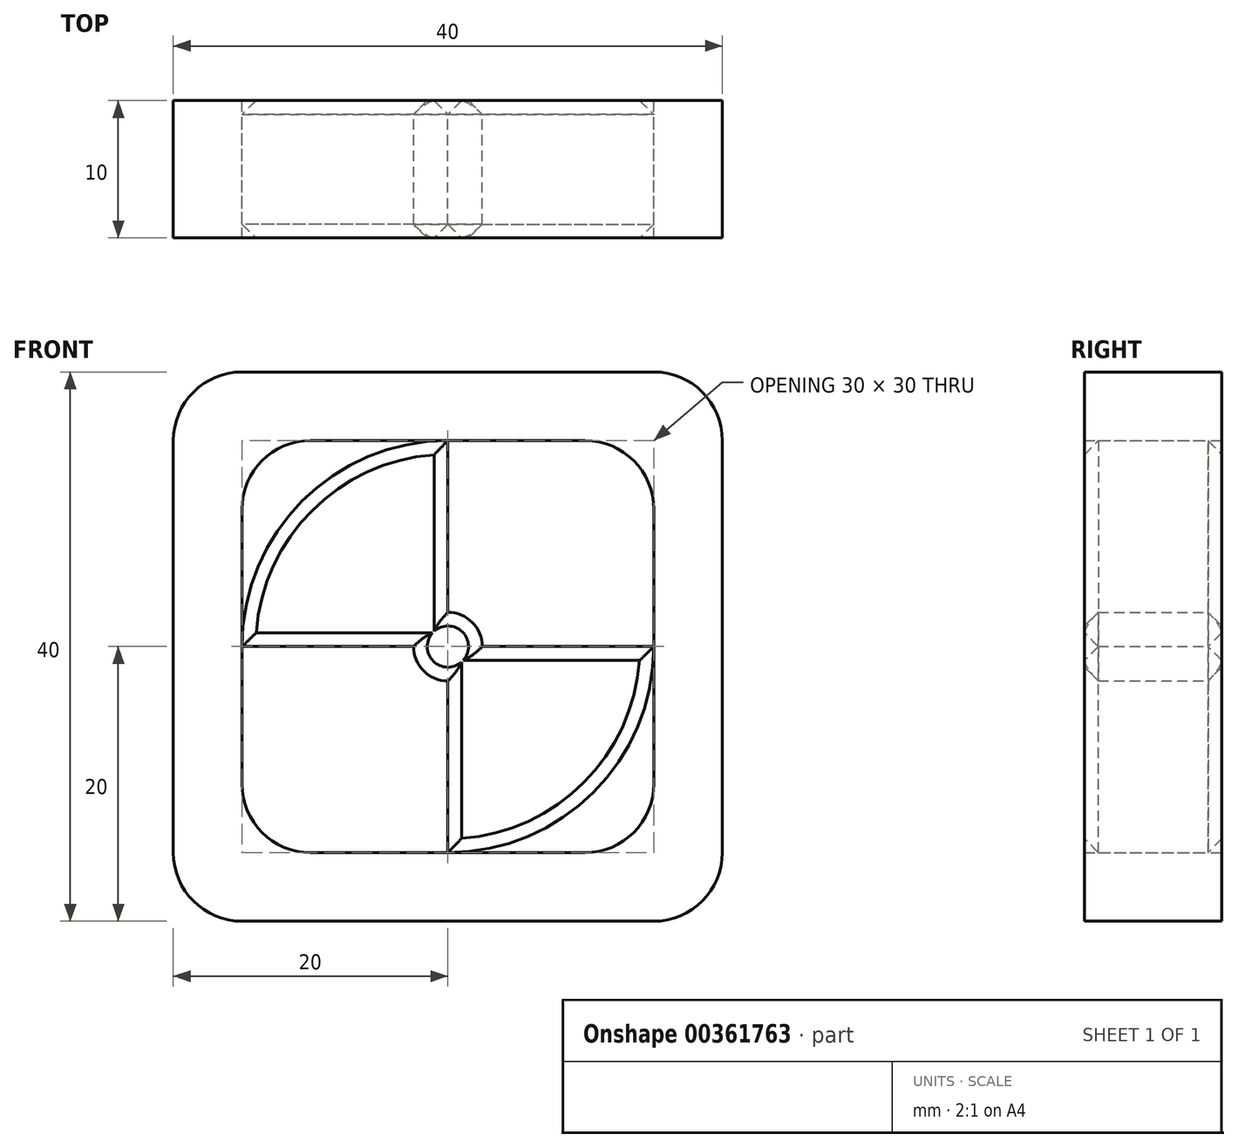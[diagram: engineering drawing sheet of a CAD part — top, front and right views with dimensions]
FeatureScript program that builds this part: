
annotation { "Feature Type Name" : "Feature", "Feature Type Description" : "" }
export const myFeature = defineFeature(function(context is Context, id is Id, definition is map)
    precondition{}
    {
        {
            var Q0;
            Q0=qCreatedBy(makeId("Front.planeOp"),FACE);
            var sketch = newSketch(context, id + "F0", { "sketchPlane" : qUnion([Q0])});
            skLineSegment(sketch, "E0.bottom", {"start": v(15, 15) * mm, "end": v(-15, 15) * mm});
            skLineSegment(sketch, "E0.top", {"start": v(15, -15) * mm, "end": v(-15, -15) * mm});
            skLineSegment(sketch, "E0.left", {"start": v(15, 15) * mm, "end": v(15, -15) * mm});
            skLineSegment(sketch, "E0.right", {"start": v(-15, 15) * mm, "end": v(-15, -15) * mm});
            skPoint(sketch, "E0.middle", {"position": v(0, 0) * mm});
            skLineSegment(sketch, "E1.bottom", {"start": v(20, 20) * mm, "end": v(-20, 20) * mm});
            skLineSegment(sketch, "E1.top", {"start": v(20, -20) * mm, "end": v(-20, -20) * mm});
            skLineSegment(sketch, "E1.left", {"start": v(20, 20) * mm, "end": v(20, -20) * mm});
            skLineSegment(sketch, "E1.right", {"start": v(-20, 20) * mm, "end": v(-20, -20) * mm});
            skCircle(sketch, "E2", {"center": v(0, 0) * mm, "radius": 15 * mm});
            skLineSegment(sketch, "E3", {"start": v(-2.5, 0) * mm, "end": v(-15, 0) * mm});
            skLineSegment(sketch, "E4", {"start": v(0, 2.5) * mm, "end": v(0, 15) * mm});
            skLineSegment(sketch, "E5", {"start": v(0, -2.5) * mm, "end": v(0, -15) * mm});
            skLineSegment(sketch, "E6", {"start": v(2.5, 0) * mm, "end": v(15, 0) * mm});
            skArc(sketch, "E7", {"start": v(2.5, 0) * mm, "mid": v(1.77, 1.77) * mm, "end": v(0, 2.5) * mm});
            skArc(sketch, "E8.trimOffspring", {"start": v(-2.5, 0) * mm, "mid": v(-1.77, -1.77) * mm, "end": v(0, -2.5) * mm});
            skSolve(sketch);
        }
        {
            var Q0;
            Q0 = qSketchRegion(id + "F0", true);
            var Q1;
            {var subQ0=sQuery(id+"F0.wireOp",EDGE,"E3");Q1=makeQuery(id+"F0.imprint","IMPRINT",FACE,{"disambiguationData":[TD([[makeQuery(id+"F0.imprint","IMPRINT",EDGE,{"derivedFrom":subQ0}),-1.0]])]});}
            var Q2;
            {var subQ0=sQuery(id+"F0.wireOp",EDGE,"E5");Q2=makeQuery(id+"F0.imprint","IMPRINT",FACE,{"disambiguationData":[TD([[makeQuery(id+"F0.imprint","IMPRINT",EDGE,{"derivedFrom":subQ0}),1.0]])]});}
            extrude(context, id + "F1", {"entities" : qUnion([Q0, Q1, Q2]), "depth" : 10 * mm});
        }
        {
            var Q0;
            Q0=makeQuery(id+"F1.opExtrude","SWEPT_EDGE",EDGE,{"disambiguationData":[OSD([sQuery(id+"F0.wireOp",EDGE,"E1.bottom"),sQuery(id+"F0.wireOp",EDGE,"E1.right")])]});
            var Q1;
            Q1=makeQuery(id+"F1.opExtrude","SWEPT_EDGE",EDGE,{"disambiguationData":[OSD([sQuery(id+"F0.wireOp",EDGE,"E1.bottom"),sQuery(id+"F0.wireOp",EDGE,"E1.left")])]});
            var Q2;
            Q2=makeQuery(id+"F1.opExtrude","SWEPT_EDGE",EDGE,{"disambiguationData":[OSD([sQuery(id+"F0.wireOp",EDGE,"E1.top"),sQuery(id+"F0.wireOp",EDGE,"E1.left")])]});
            var Q3;
            Q3=makeQuery(id+"F1.opExtrude","SWEPT_EDGE",EDGE,{"disambiguationData":[OSD([sQuery(id+"F0.wireOp",EDGE,"E1.top"),sQuery(id+"F0.wireOp",EDGE,"E1.right")])]});
            var Q4;
            Q4=makeQuery(id+"F1.opExtrude","SWEPT_EDGE",EDGE,{"disambiguationData":[OSD([sQuery(id+"F0.wireOp",EDGE,"E0.top"),sQuery(id+"F0.wireOp",EDGE,"E0.left")])]});
            var Q5;
            Q5=makeQuery(id+"F1.opExtrude","SWEPT_EDGE",EDGE,{"disambiguationData":[OSD([sQuery(id+"F0.wireOp",EDGE,"E0.bottom"),sQuery(id+"F0.wireOp",EDGE,"E0.left")])]});
            var Q6;
            Q6=makeQuery(id+"F1.opExtrude","SWEPT_EDGE",EDGE,{"disambiguationData":[OSD([sQuery(id+"F0.wireOp",EDGE,"E0.top"),sQuery(id+"F0.wireOp",EDGE,"E0.right")])]});
            var Q7;
            Q7=makeQuery(id+"F1.opExtrude","SWEPT_EDGE",EDGE,{"disambiguationData":[OSD([sQuery(id+"F0.wireOp",EDGE,"E0.bottom"),sQuery(id+"F0.wireOp",EDGE,"E0.right")])]});
            fillet(context, id + "F2", {"entities" : qUnion([Q0, Q1, Q2, Q3, Q4, Q5, Q6, Q7]), "radius" : 5 * mm, "tangentPropagation" : true, "allowEdgeOverflow" : false});
        }
        {
            var Q0;
            Q0=makeQuery(id+"F1.opExtrude","CAP_FACE",FACE,{"disambiguationData":[OSD([sQuery(id+"F0.wireOp",EDGE,"E2"),sQuery(id+"F0.wireOp",EDGE,"E3"),sQuery(id+"F0.wireOp",EDGE,"E4"),sQuery(id+"F0.wireOp",EDGE,"E5"),sQuery(id+"F0.wireOp",EDGE,"E6"),sQuery(id+"F0.wireOp",EDGE,"E7"),sQuery(id+"F0.wireOp",EDGE,"E8.trimOffspring")])],"isStart":true});
            chamfer(context, id + "F3", {"entities" : qUnion([Q0]), "width" : 1 * mm, "tangentPropagation" : true});
        }
        {
            var Q0;
            Q0=makeQuery(id+"F1.opExtrude","CAP_FACE",FACE,{"disambiguationData":[OSD([sQuery(id+"F0.wireOp",EDGE,"E2"),sQuery(id+"F0.wireOp",EDGE,"E3"),sQuery(id+"F0.wireOp",EDGE,"E4"),sQuery(id+"F0.wireOp",EDGE,"E5"),sQuery(id+"F0.wireOp",EDGE,"E6"),sQuery(id+"F0.wireOp",EDGE,"E7"),sQuery(id+"F0.wireOp",EDGE,"E8.trimOffspring")])],"isStart":false});
            chamfer(context, id + "F4", {"entities" : qUnion([Q0]), "width" : 1 * mm, "tangentPropagation" : true});
        }
    });
